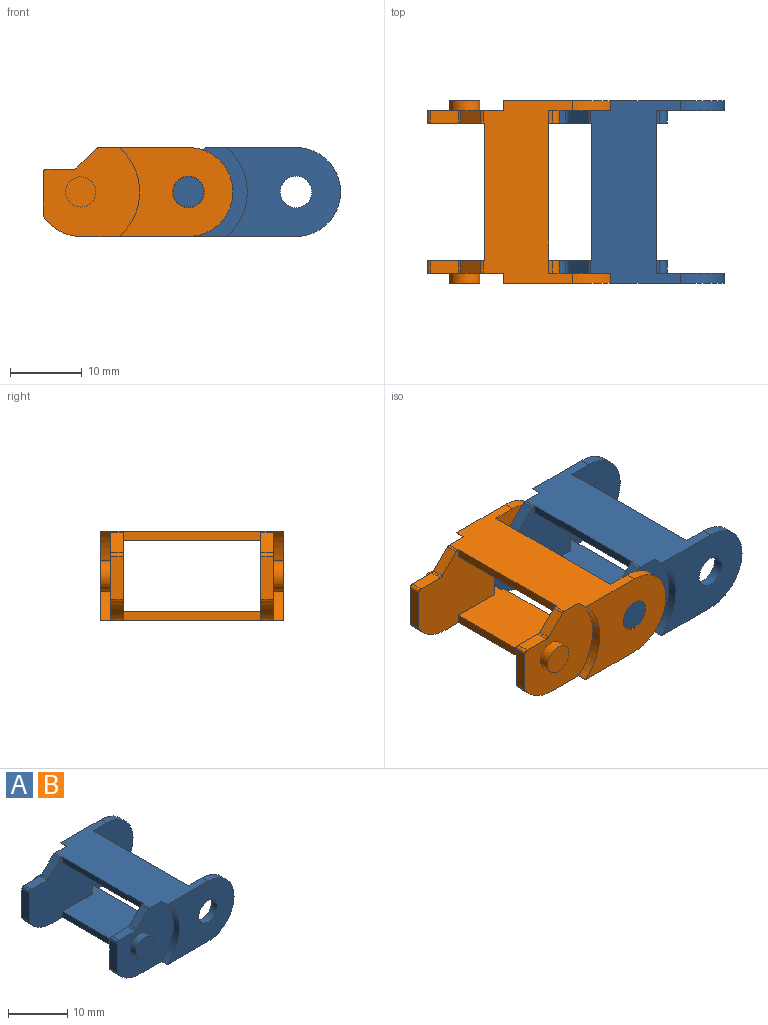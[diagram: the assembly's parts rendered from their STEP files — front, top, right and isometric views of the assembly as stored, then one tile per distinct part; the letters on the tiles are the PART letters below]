
ASSEMBLY  parts=2 mates=1
PART A: 50 faces, bbox 26.4x25.4x12.4 mm
  f0: plane 12.4x11.4mm, normal (0,-1,0), area 98.7mm2, adj f1,f2,f3,f5,f7,f11,f13,f19
  f1: plane 25.4x15mm, normal (0,0,-1), area 239.6mm2, adj f0,f2,f4,f6,f10,f12,f13,f14
  f2: cylinder r=6.2mm len=12.4mm, axis (0,1,0), area 27.3mm2, adj f0,f1,f3,f6
  f3: plane 25.4x12.43mm, normal (0,0,1), area 230.8mm2, adj f0,f2,f4,f6,f7,f8,f10,f14
  f4: cylinder r=8.2mm len=12.4mm, axis (0,1,0), area 19.7mm2, adj f1,f3,f6,f10
  f5: cylinder r=2.2mm len=4.4mm, axis (0,1,0), area 19.4mm2, adj f0,f6
  f6: plane 15.83x12.4mm, normal (0,1,0), area 140.3mm2, adj f1,f2,f3,f4,f5
  f7: plane 22.6x1.2mm, normal (1,0,0), area 27.1mm2, adj f0,f3,f9,f21,f29,f42
  f8: plane 19.2x1.2mm, normal (-1,0,0), area 23mm2, adj f3,f9,f14,f35
  f9: plane 19.2x9mm, normal (0,0,-1), area 172.8mm2, adj f7,f8,f14,f35
  f10: plane 13.4x12.4mm, normal (0,1,0), area 119.1mm2, adj f1,f3,f4,f15,f16,f17,f18,f22
  f11: plane 22.6x9mm, normal (0,0,1), area 179.3mm2, adj f0,f12,f13,f14,f19,f29,f35,f40
  f12: plane 19.2x1.2mm, normal (-1,0,0), area 23mm2, adj f1,f11,f14,f35
  f13: plane 22.6x1.2mm, normal (1,0,0), area 27.1mm2, adj f0,f1,f11,f29
  f14: plane 18.4x12.4mm, normal (0,-1,0), area 152.8mm2, adj f1,f3,f8,f9,f11,f12,f15,f16
  f15: plane 2.78x2.72mm, normal (-0.7,0,0.71), area 6.6mm2, adj f10,f14,f24,f25
  f16: plane 3.8x1.7mm, normal (0,0,1), area 6.5mm2, adj f10,f14,f25,f26
  f17: plane 5.93x1.7mm, normal (-1,0,0), area 10.1mm2, adj f10,f14,f26,f27
  f18: cylinder r=6.2mm len=5.11mm, axis (0,1,0), area 10.2mm2, adj f1,f10,f14,f27
  f19: plane 8x1.7mm, normal (1,0,0), area 13.6mm2, adj f0,f11,f14,f20
  f20: plane 2.4x1.7mm, normal (0,0,-1), area 4.1mm2, adj f0,f14,f19,f28
  f21: plane 1.7x0.5mm, normal (0,0,1), area 0.8mm2, adj f0,f7,f14,f28
  f22: cylinder r=2.1mm len=4.2mm, axis (0,1,0), area 18.5mm2, adj f10,f23
  f23: plane 4.2x4.2mm, normal (0,1,0), area 13.9mm2, adj f22
  f24: cylinder r=0.5mm len=1.7mm, axis (0,-1,0), area 0.7mm2, adj f3,f10,f14,f15
  f25: cylinder r=0.5mm len=1.7mm, axis (0,1,0), area 0.7mm2, adj f10,f14,f15,f16
  f26: cylinder r=0.5mm len=1.7mm, axis (0,-1,0), area 1.3mm2, adj f10,f14,f16,f17
  f27: cylinder r=0.5mm len=1.7mm, axis (0,1,0), area 0.5mm2, adj f10,f14,f17,f18
  f28: cylinder r=1mm len=2mm, axis (0,-1,0), area 5.3mm2, adj f0,f14,f20,f21
  f29: plane 12.4x11.4mm, normal (0,1,0), area 98.7mm2, adj f1,f3,f7,f11,f13,f30,f32,f40
  f30: cylinder r=6.2mm len=12.4mm, axis (0,-1,0), area 27.3mm2, adj f1,f3,f29,f33
  f31: cylinder r=8.2mm len=12.4mm, axis (0,-1,0), area 19.7mm2, adj f1,f3,f33,f34
  f32: cylinder r=2.2mm len=4.4mm, axis (0,-1,0), area 19.4mm2, adj f29,f33
  f33: plane 15.83x12.4mm, normal (0,-1,0), area 140.3mm2, adj f1,f3,f30,f31,f32
  f34: plane 13.4x12.4mm, normal (0,-1,0), area 119.1mm2, adj f1,f3,f31,f36,f37,f38,f39,f43
  f35: plane 18.4x12.4mm, normal (0,1,0), area 152.8mm2, adj f1,f3,f8,f9,f11,f12,f36,f37
  f36: plane 2.78x2.72mm, normal (-0.7,0,0.71), area 6.6mm2, adj f34,f35,f45,f46
  f37: plane 3.8x1.7mm, normal (0,0,1), area 6.5mm2, adj f34,f35,f46,f47
  f38: plane 5.93x1.7mm, normal (-1,0,0), area 10.1mm2, adj f34,f35,f47,f48
  f39: cylinder r=6.2mm len=5.11mm, axis (0,-1,0), area 10.2mm2, adj f1,f34,f35,f48
  f40: plane 8x1.7mm, normal (1,0,0), area 13.6mm2, adj f11,f29,f35,f41
  f41: plane 2.4x1.7mm, normal (0,0,-1), area 4.1mm2, adj f29,f35,f40,f49
  f42: plane 1.7x0.5mm, normal (0,0,1), area 0.8mm2, adj f7,f29,f35,f49
  f43: cylinder r=2.1mm len=4.2mm, axis (0,-1,0), area 18.5mm2, adj f34,f44
  f44: plane 4.2x4.2mm, normal (0,-1,0), area 13.9mm2, adj f43
  f45: cylinder r=0.5mm len=1.7mm, axis (0,1,0), area 0.7mm2, adj f3,f34,f35,f36
  f46: cylinder r=0.5mm len=1.7mm, axis (0,-1,0), area 0.7mm2, adj f34,f35,f36,f37
  f47: cylinder r=0.5mm len=1.7mm, axis (0,1,0), area 1.3mm2, adj f34,f35,f37,f38
  f48: cylinder r=0.5mm len=1.7mm, axis (0,-1,0), area 0.5mm2, adj f34,f35,f38,f39
  f49: cylinder r=1mm len=2mm, axis (0,1,0), area 5.3mm2, adj f29,f35,f41,f42
PART B: same geometry as A
PLACE A t=(15,0,0)mm
PLACE B at identity
MATE revolute A.f22 <-> B.f5  axis (0,-1,0) through (7,-25.4,0)mm
